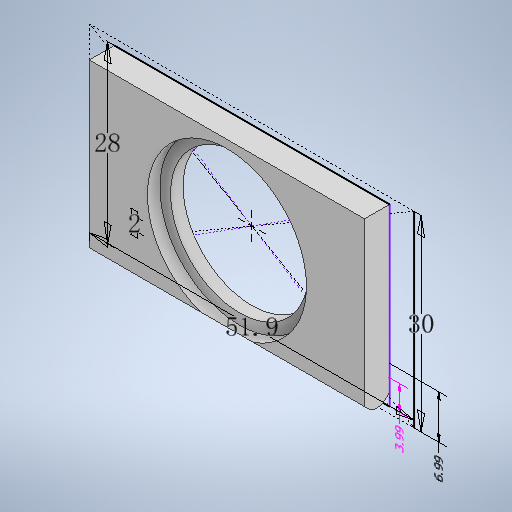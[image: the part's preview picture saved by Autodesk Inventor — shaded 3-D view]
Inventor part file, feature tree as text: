
AUTODESK INVENTOR PART (.ipt)
format: ipt  version: 2025 (Build 290162000, 162)  size: 299,008 bytes
history: native  units: mm
features: sketch x2, hole x2, other x2, extrude x1, chamfer x1, fillet x1
ambient origin geometry x8: Origin, YZ Plane, XZ Plane, XY Plane, X Axis, Y Axis, Z Axis, Center Point
bodies: 实体1 (feature_tree)
feature tree (9):
  sketch  "草图1"  dims[d0=51.9mm d1=30.0mm]
  extrude  "拉伸1"  Depth=30.0mm
  hole  "孔1"  [1 undecoded]
  hole  "孔2"  [1 undecoded]
  chamfer  "倒角1"  Distance=2.0mm
  fillet  "圆角1"  Radius=2.0mm
  sketch  "草图2"  dims[d6=28.0mm d7=4.0mm d8=0.0mm d9=4.95mm d10=6.0mm d11=4.0mm d12=2.0mm d13=90.0deg d14=2.5mm d15=20.594885mm d16=22.0mm d17=6.0mm d18=25.4mm d19=2.0mm d20=90.0deg d21=0.5mm d22=20.594885mm d27=2.0mm d28=2.0mm d29=2.0mm d30=45.0deg d31=2.0mm d24=8.608462mm d25=3.991113mm d32=8.081937mm d33=6.991113mm d23=1.0mm d26=0.15mm d34=0.375mm d35=0.375mm]
  other  "线性尺寸 1"
  other  "线性尺寸 2"
note: 2 required parameter values undecoded (feature->parameter linkage not recoverable at this tier; creation-order binding heuristic only, values carry confidence <= 0.55)
